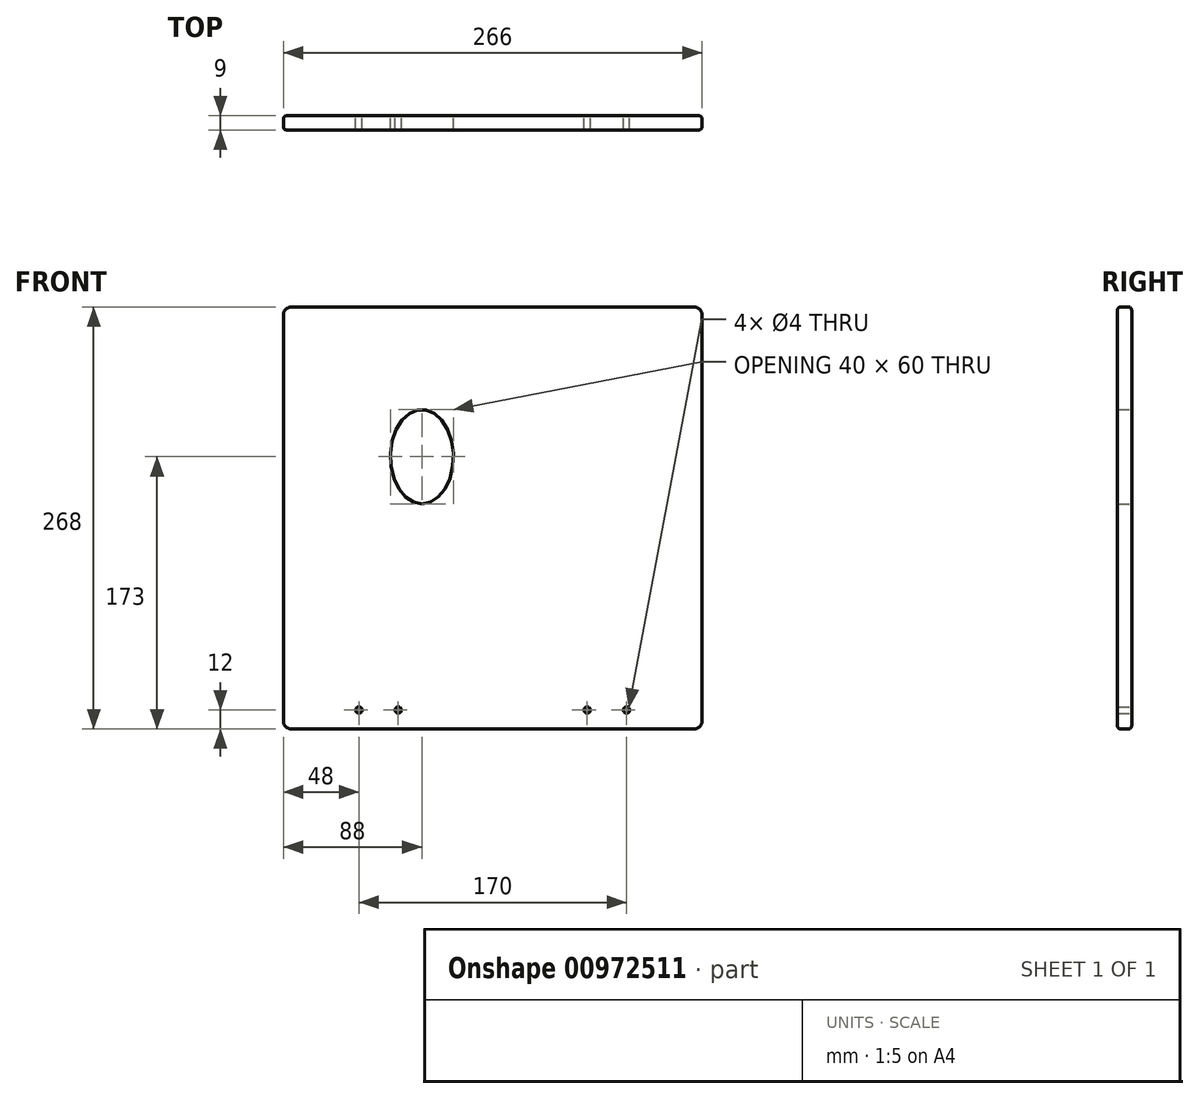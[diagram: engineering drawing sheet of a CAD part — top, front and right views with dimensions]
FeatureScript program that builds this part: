
annotation { "Feature Type Name" : "Feature", "Feature Type Description" : "" }
export const myFeature = defineFeature(function(context is Context, id is Id, definition is map)
    precondition{}
    {
        {
            var Q0;
            Q0=qCreatedBy(makeId("Front.planeOp"),FACE);
            var sketch = newSketch(context, id + "F0", { "sketchPlane" : qUnion([Q0])});
            skLineSegment(sketch, "E0.top", {"start": v(-133, 0) * mm, "end": v(133, 0) * mm});
            skLineSegment(sketch, "E0.left", {"start": v(-133, 268) * mm, "end": v(-133, 0) * mm});
            skLineSegment(sketch, "E0.right", {"start": v(133, 268) * mm, "end": v(133, 0) * mm});
            skLineSegment(sketch, "E1", {"start": v(-133, 268) * mm, "end": v(133, 268) * mm});
            skSolve(sketch);
        }
        {
            var Q0;
            Q0=makeQuery(id+"F0.imprint","IMPRINT",FACE,{"disambiguationData":[TD([[makeQuery(id+"F0.imprint","IMPRINT",EDGE,{"derivedFrom":sQuery(id+"F0.wireOp",EDGE,"E0.top")}),1.0]])]});
            extrude(context, id + "F1", {"entities" : qUnion([Q0]), "depth" : 9 * mm, "offsetDistance" : 25 * mm});
        }
        {
            var Q0;
            Q0=qCreatedBy(makeId("Front.planeOp"),FACE);
            var sketch = newSketch(context, id + "F2", { "sketchPlane" : qUnion([Q0])});
            skEllipse(sketch, "E2", {"center": v(-45, 173) * mm, "majorRadius": 30 * mm, "minorRadius": 20 * mm, "majorAxis": v(0, -1)});
            skLineSegment(sketch, "E3", {"start": v(-45, 173) * mm, "end": v(-45, 268) * mm, "construction": true});
            skLineSegment(sketch, "E4", {"start": v(-45, 173) * mm, "end": v(-45, 0) * mm, "construction": true});
            skSolve(sketch);
        }
        {
            var Q0;
            Q0=qSketchRegion(id+"F2",true);
            extrude(context, id + "F3", {"entities" : qUnion([Q0]), "operationType" : NewBodyOperationType.REMOVE, "endBound" : BoundingType.THROUGH_ALL, "depth" : 25 * mm, "offsetDistance" : 25 * mm});
        }
        {
            var Q0;
            Q0=makeQuery(id+"F1.opExtrude","SWEPT_EDGE",EDGE,{"disambiguationData":[OSD([sQuery(id+"F0.wireOp",EDGE,"E0.top"),sQuery(id+"F0.wireOp",EDGE,"E0.right")])]});
            var Q1;
            Q1=makeQuery(id+"F1.opExtrude","SWEPT_EDGE",EDGE,{"disambiguationData":[OSD([sQuery(id+"F0.wireOp",EDGE,"E0.top"),sQuery(id+"F0.wireOp",EDGE,"E0.left")])]});
            var Q2;
            Q2=makeQuery(id+"F1.opExtrude","SWEPT_EDGE",EDGE,{"disambiguationData":[OSD([sQuery(id+"F0.wireOp",EDGE,"9Qd7OF7F-3ocl-s4x1-BWDE-BtM8wvj1FX4r"),sQuery(id+"F0.wireOp",EDGE,"ll6YLceh-0rU6-i4zH-WBJZ-I9S6CAPv5mTM")])]});
            var Q3;
            Q3=makeQuery(id+"F1.opExtrude","SWEPT_EDGE",EDGE,{"disambiguationData":[OSD([sQuery(id+"F0.wireOp",EDGE,"ll6YLceh-0rU6-i4zH-WBJZ-I9S6CAPv5mTM"),sQuery(id+"F0.wireOp",EDGE,"7YbRFc1p-xvI9-C5Bv-h4iq-wk3zZMqcf456")])]});
            var Q4;
            Q4=makeQuery(id+"F1.opExtrude","SWEPT_EDGE",EDGE,{"disambiguationData":[OSD([sQuery(id+"F0.wireOp",EDGE,"E0.top"),sQuery(id+"F0.wireOp",EDGE,"E0.left")])]});
            var Q5;
            Q5=makeQuery(id+"F1.opExtrude","SWEPT_EDGE",EDGE,{"disambiguationData":[OSD([sQuery(id+"F0.wireOp",EDGE,"E0.top"),sQuery(id+"F0.wireOp",EDGE,"E0.right")])]});
            var Q6;
            Q6=makeQuery(id+"F1.opExtrude","SWEPT_EDGE",EDGE,{"disambiguationData":[OSD([sQuery(id+"F0.wireOp",EDGE,"LukqBGKj-ALpC-M4hR-kFol-LkI75Zf4n1DU"),sQuery(id+"F0.wireOp",EDGE,"ftUaj2uN-i1qy-vV0B-sOZa-NXubvh63IMu2")])]});
            var Q7;
            Q7=makeQuery(id+"F1.opExtrude","SWEPT_EDGE",EDGE,{"disambiguationData":[OSD([sQuery(id+"F0.wireOp",EDGE,"ftUaj2uN-i1qy-vV0B-sOZa-NXubvh63IMu2"),sQuery(id+"F0.wireOp",EDGE,"eMYpGBdX-C2kL-OgRv-d0g4-F0ux3sYP1lq8")])]});
            var Q8;
            Q8=makeQuery(id+"F1.opExtrude","SWEPT_EDGE",EDGE,{"disambiguationData":[OSD([sQuery(id+"F0.wireOp",EDGE,"E0.right"),sQuery(id+"F0.wireOp",EDGE,"E1")])]});
            var Q9;
            Q9=makeQuery(id+"F1.opExtrude","SWEPT_EDGE",EDGE,{"disambiguationData":[OSD([sQuery(id+"F0.wireOp",EDGE,"E0.left"),sQuery(id+"F0.wireOp",EDGE,"E1")])]});
            fillet(context, id + "F4", {"entities" : qUnion([Q0, Q1, Q2, Q3, Q4, Q5, Q6, Q7, Q8, Q9]), "radius" : 5 * mm, "tangentPropagation" : true, "allowEdgeOverflow" : false});
        }
        {
            var Q0;
            Q0=makeQuery(id+"F1.opExtrude","CAP_EDGE",EDGE,{"disambiguationData":[OSD([sQuery(id+"F0.wireOp",EDGE,"E0.top")])],"isStart":false});
            var Q1;
            Q1=makeQuery(id+"F1.opExtrude","CAP_EDGE",EDGE,{"disambiguationData":[OSD([sQuery(id+"F0.wireOp",EDGE,"E0.top")])],"isStart":true});
            var Q2;
            Q2=makeQuery(id+"F3.boolean.opBoolean","INTERSECT",EDGE,{"derivedFrom":[makeQuery(id+"F1.opExtrude","CAP_FACE",FACE,{"disambiguationData":[OSD([sQuery(id+"F0.wireOp",EDGE,"E0.bottom"),sQuery(id+"F0.wireOp",EDGE,"E0.top"),sQuery(id+"F0.wireOp",EDGE,"E0.left"),sQuery(id+"F0.wireOp",EDGE,"E0.right")])],"isStart":false}),makeQuery(id+"F3.opExtrude","SWEPT_FACE",FACE,{"disambiguationData":[OSD([sQuery(id+"F2.wireOp",EDGE,"aTs2lwnH-bZmC-Yp0V-wstF-OkDp7FbwyCUC")])]})]});
            var Q3;
            Q3=makeQuery(id+"F3.boolean.opBoolean","COPY",EDGE,{"derivedFrom":makeQuery(id+"F3.opExtrude","CAP_EDGE",EDGE,{"disambiguationData":[OSD([sQuery(id+"F2.wireOp",EDGE,"aTs2lwnH-bZmC-Yp0V-wstF-OkDp7FbwyCUC")])],"isStart":true})});
            var Q4;
            Q4=makeQuery(id+"Fau0sHsyIT94Q2H_1.1.F3.boolean.opBoolean","INTERSECT",EDGE,{"derivedFrom":[makeQuery(id+"F1.opExtrude","CAP_FACE",FACE,{"disambiguationData":[OSD([sQuery(id+"F0.wireOp",EDGE,"E0.bottom"),sQuery(id+"F0.wireOp",EDGE,"E0.top"),sQuery(id+"F0.wireOp",EDGE,"E0.left"),sQuery(id+"F0.wireOp",EDGE,"E0.right")])],"isStart":false}),makeQuery(id+"Fau0sHsyIT94Q2H_1.1.F3.opExtrude","SWEPT_FACE",FACE,{"disambiguationData":[OSD([sQuery(id+"F2.wireOp",EDGE,"aTs2lwnH-bZmC-Yp0V-wstF-OkDp7FbwyCUC")])]})]});
            var Q5;
            Q5=makeQuery(id+"Fau0sHsyIT94Q2H_1.1.F3.boolean.opBoolean","COPY",EDGE,{"derivedFrom":makeQuery(id+"Fau0sHsyIT94Q2H_1.1.F3.opExtrude","CAP_EDGE",EDGE,{"disambiguationData":[OSD([sQuery(id+"F2.wireOp",EDGE,"aTs2lwnH-bZmC-Yp0V-wstF-OkDp7FbwyCUC")])],"isStart":true})});
            var Q6;
            Q6=makeQuery(id+"F1.opExtrude","CAP_EDGE",EDGE,{"disambiguationData":[OSD([sQuery(id+"F0.wireOp",EDGE,"9Qd7OF7F-3ocl-s4x1-BWDE-BtM8wvj1FX4r")])],"isStart":false});
            var Q7;
            Q7=makeQuery(id+"F1.opExtrude","CAP_EDGE",EDGE,{"disambiguationData":[OSD([sQuery(id+"F0.wireOp",EDGE,"9Qd7OF7F-3ocl-s4x1-BWDE-BtM8wvj1FX4r")])],"isStart":true});
            var Q8;
            Q8=makeQuery(id+"F3.boolean.opBoolean","COPY",EDGE,{"derivedFrom":makeQuery(id+"F3.opExtrude","CAP_EDGE",EDGE,{"disambiguationData":[OSD([sQuery(id+"F2.wireOp",EDGE,"E2")])],"isStart":true})});
            var Q9;
            Q9=makeQuery(id+"Fau0sHsyIT94Q2H_1.1.F3.boolean.opBoolean","COPY",EDGE,{"derivedFrom":makeQuery(id+"Fau0sHsyIT94Q2H_1.1.F3.opExtrude","CAP_EDGE",EDGE,{"disambiguationData":[OSD([sQuery(id+"F2.wireOp",EDGE,"E2")])],"isStart":true})});
            var Q10;
            Q10=makeQuery(id+"F1.opExtrude","CAP_EDGE",EDGE,{"disambiguationData":[OSD([sQuery(id+"F0.wireOp",EDGE,"ftUaj2uN-i1qy-vV0B-sOZa-NXubvh63IMu2")])],"isStart":false});
            var Q11;
            Q11=makeQuery(id+"F1.opExtrude","CAP_EDGE",EDGE,{"disambiguationData":[OSD([sQuery(id+"F0.wireOp",EDGE,"ftUaj2uN-i1qy-vV0B-sOZa-NXubvh63IMu2")])],"isStart":true});
            fillet(context, id + "F5", {"entities" : qUnion([Q0, Q1, Q2, Q3, Q4, Q5, Q6, Q7, Q8, Q9, Q10, Q11]), "radius" : 2 * mm, "tangentPropagation" : true, "allowEdgeOverflow" : false});
        }
        {
            var Q0;
            Q0=qCreatedBy(makeId("Front.planeOp"),FACE);
            var sketch = newSketch(context, id + "F6", { "sketchPlane" : qUnion([Q0])});
            skPoint(sketch, "E5", {"position": v(-85, 12) * mm});
            skPoint(sketch, "E6", {"position": v(-60, 12) * mm});
            skPoint(sketch, "E7", {"position": v(60, 12) * mm});
            skPoint(sketch, "E8", {"position": v(85, 12) * mm});
            skLineSegment(sketch, "E9", {"start": v(-85, 12) * mm, "end": v(-60, 12) * mm, "construction": true});
            skLineSegment(sketch, "E10", {"start": v(-60, 12) * mm, "end": v(60, 12) * mm, "construction": true});
            skLineSegment(sketch, "E11", {"start": v(60, 12) * mm, "end": v(85, 12) * mm, "construction": true});
            skLineSegment(sketch, "E12", {"start": v(0, 0) * mm, "end": v(0, 12) * mm, "construction": true});
            skSolve(sketch);
        }
        {
            var Q0;
            Q0=sQuery(id+"F6.wireOp",VERTEX,"E5");
            var Q1;
            Q1=sQuery(id+"F6.wireOp",VERTEX,"E9.end");
            var Q2;
            Q2=sQuery(id+"F6.wireOp",VERTEX,"E7");
            var Q3;
            Q3=sQuery(id+"F6.wireOp",VERTEX,"E8");
            var Q4;
            Q4=makeQuery(id+"F1.opExtrude","SWEPT_BODY",BODY,{"disambiguationData":[OSD([sQuery(id+"F0.wireOp",EDGE,"E0.top"),sQuery(id+"F0.wireOp",EDGE,"E0.left"),sQuery(id+"F0.wireOp",EDGE,"E0.right"),sQuery(id+"F0.wireOp",EDGE,"E1")])]});
            hole(context, id + "F7", {"style" : HoleStyle.SIMPLE, "endStyle" : HoleEndStyle.THROUGH, "oppositeDirection" : true, "holeDiameter" : 4 * mm, "majorDiameter" : 5 * mm, "isTappedThrough" : true, "tappedDepth" : 12 * mm, "tapClearance" : 3, "locations" : qUnion([Q0, Q1, Q2, Q3]), "scope" : qUnion([Q4])});
        }
    });
